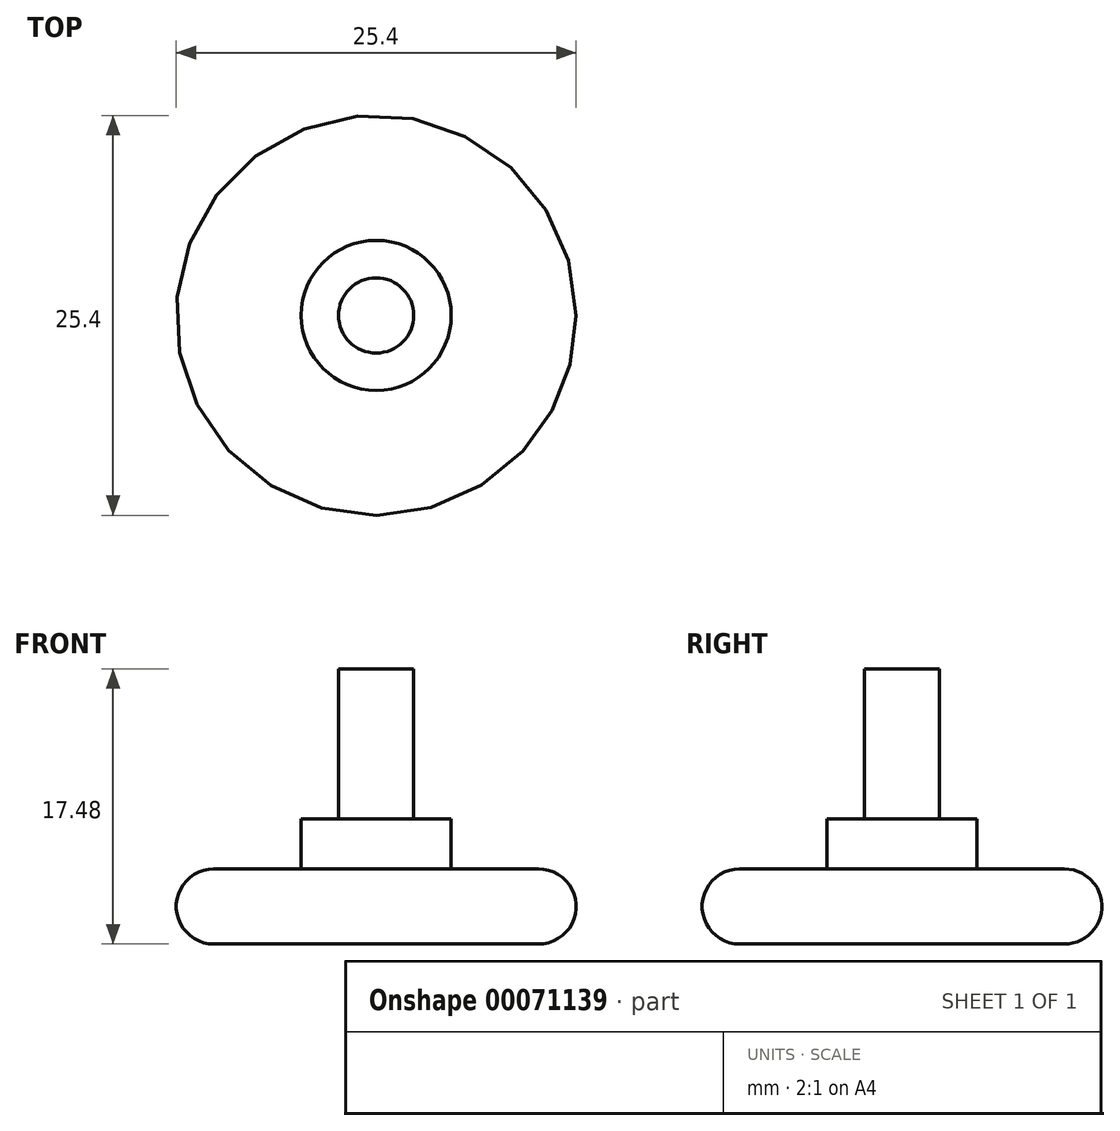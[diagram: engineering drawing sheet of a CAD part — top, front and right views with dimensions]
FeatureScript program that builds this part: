
annotation { "Feature Type Name" : "Feature", "Feature Type Description" : "" }
export const myFeature = defineFeature(function(context is Context, id is Id, definition is map)
    precondition{}
    {
        {
            var Q0;
            Q0=qCreatedBy(makeId("Front.planeOp"),FACE);
            var sketch = newSketch(context, id + "F0", { "sketchPlane" : qUnion([Q0])});
            skLineSegment(sketch, "E0.bottom", {"start": v(-13.98, 3.82) * mm, "end": v(-1.28, 3.82) * mm});
            skLineSegment(sketch, "E0.top", {"start": v(-13.98, -0.96) * mm, "end": v(-1.28, -0.96) * mm});
            skLineSegment(sketch, "E0.left", {"start": v(-13.98, 3.82) * mm, "end": v(-13.98, -0.96) * mm});
            skLineSegment(sketch, "E0.right", {"start": v(-1.28, 3.82) * mm, "end": v(-1.28, -0.96) * mm});
            skSolve(sketch);
        }
        {
            var Q0;
            Q0=makeQuery(id+"F0.imprint","IMPRINT",FACE,{"disambiguationData":[TD([[makeQuery(id+"F0.imprint","IMPRINT",EDGE,{"derivedFrom":sQuery(id+"F0.wireOp",EDGE,"E0.bottom")}),-1.0]])]});
            var Q1;
            Q1=sQuery(id+"F0.wireOp",EDGE,"E0.left");
            revolve(context, id + "F1", {"entities" : qUnion([Q0]), "axis" : qUnion([Q1]), "revolveType" : RevolveType.FULL});
        }
        {
            var Q0;
            Q0=makeQuery(id+"F1.opRevolve","SWEPT_FACE",FACE,{"disambiguationData":[OSD([sQuery(id+"F0.wireOp",EDGE,"E0.right")])]});
            var Q1;
            Q1=makeQuery(id+"F1.opRevolve","SWEPT_EDGE",EDGE,{"disambiguationData":[OSD([sQuery(id+"F0.wireOp",EDGE,"E0.top"),sQuery(id+"F0.wireOp",EDGE,"E0.right")])]});
            fillet(context, id + "F2", {"entities" : qUnion([Q0, Q1]), "radius" : 2.4 * mm, "tangentPropagation" : true, "allowEdgeOverflow" : false});
        }
        {
            var Q0;
            Q0=makeQuery(id+"F1.opRevolve","SWEPT_FACE",FACE,{"disambiguationData":[OSD([sQuery(id+"F0.wireOp",EDGE,"E0.bottom")])]});
            var sketch = newSketch(context, id + "F3", { "sketchPlane" : qUnion([Q0])});
            skCircle(sketch, "E1", {"center": v(-13.98, 0) * mm, "radius": 4.76 * mm});
            skSolve(sketch);
        }
        {
            var Q0;
            Q0=makeQuery(id+"F3.imprint","IMPRINT",FACE,{"disambiguationData":[TD([[makeQuery(id+"F3.imprint","IMPRINT",EDGE,{"derivedFrom":sQuery(id+"F3.wireOp",EDGE,"E1")}),1.0]])]});
            extrude(context, id + "F4", {"entities" : qUnion([Q0]), "operationType" : NewBodyOperationType.ADD, "depth" : 3.17 * mm});
        }
        {
            var Q0;
            Q0=makeQuery(id+"F4.opExtrude","CAP_FACE",FACE,{"disambiguationData":[OSD([sQuery(id+"F3.wireOp",EDGE,"E1")])],"isStart":false});
            var sketch = newSketch(context, id + "F5", { "sketchPlane" : qUnion([Q0])});
            skCircle(sketch, "E2", {"center": v(-13.98, 0) * mm, "radius": 2.39 * mm});
            skSolve(sketch);
        }
        {
            var Q0;
            Q0 = qSketchRegion(id + "F5", true);
            extrude(context, id + "F6", {"entities" : qUnion([Q0]), "operationType" : NewBodyOperationType.ADD, "depth" : 9.52 * mm});
        }
    });
